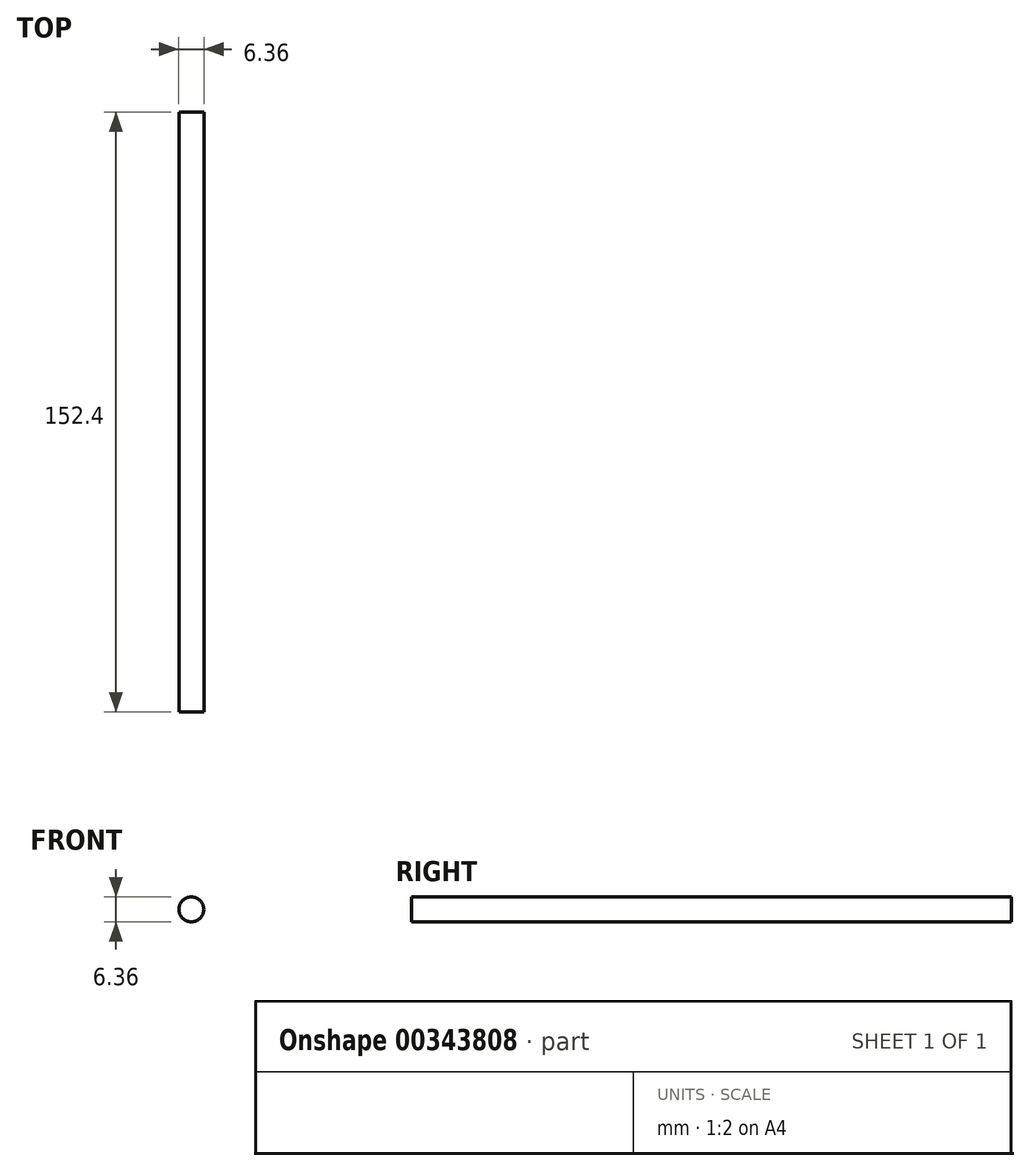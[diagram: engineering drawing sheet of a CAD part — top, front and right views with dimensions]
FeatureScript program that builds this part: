
annotation { "Feature Type Name" : "Feature", "Feature Type Description" : "" }
export const myFeature = defineFeature(function(context is Context, id is Id, definition is map)
    precondition{}
    {
        {
            var Q0;
            Q0=qCreatedBy(makeId("Front.planeOp"),FACE);
            var sketch = newSketch(context, id + "F0", { "sketchPlane" : qUnion([Q0])});
            skCircle(sketch, "E0", {"center": v(0, 0) * mm, "radius": 3.17 * mm});
            skSolve(sketch);
        }
        {
            var Q0;
            Q0 = qSketchRegion(id + "F0", true);
            extrude(context, id + "F1", {"entities" : qUnion([Q0]), "endBound" : BoundingType.SYMMETRIC, "oppositeDirection" : true, "depth" : 152.4 * mm});
        }
    });
